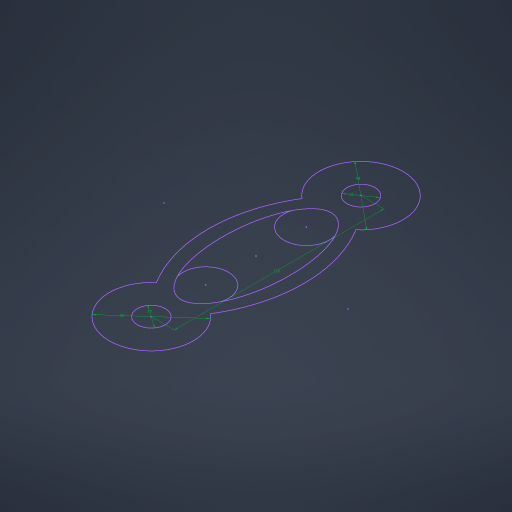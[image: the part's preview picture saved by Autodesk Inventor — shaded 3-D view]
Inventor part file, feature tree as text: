
AUTODESK INVENTOR PART (.ipt)
format: ipt  version: 2024.3 (Build 283343000, 343)  size: 191,488 bytes
history: native  units: mm
features: sketch x1
ambient origin geometry x8: Origin, YZ Plane, XZ Plane, XY Plane, X Axis, Y Axis, Z Axis, Center Point
feature tree (1):
  sketch  "Sketch1"  dims[d0=16.0mm d1=16.0mm d2=120.0mm d4=48.0mm d5=48.0mm d20=0.872665mm d21=0.872665mm d22=0.5mm d23=0.872665mm d24=0.5mm d25=0.872665mm]
